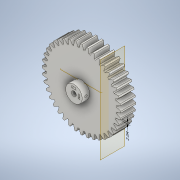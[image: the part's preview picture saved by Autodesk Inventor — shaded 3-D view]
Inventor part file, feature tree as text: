
AUTODESK INVENTOR PART (.ipt)
format: ipt  version: 2020 (Build 240168000, 168)  size: 377,344 bytes
history: native  units: mm (DEFAULTED — no unit token found)
features: sketch x7, extrude x6, other x5, plane x5
ambient origin geometry x8: Origin, YZ Plane, XZ Plane, XY Plane, X Axis, Y Axis, Z Axis, Center Point
bodies: Solid1 (feature_tree)
feature tree (23):
  other  "Annotations"
  extrude  "Extrusion1"  Depth=20.0mm TaperAngle=0.0deg
  plane  "Work Plane2"
  plane  "Work Plane8"
  plane  "Work Plane9"
  other  "Spur Gear"
  extrude  "Extrusion2"  Depth=10.0mm TaperAngle=0.0deg
  plane  "Work Plane13"
  extrude  "Extrusion3"  Depth=0.785398mm TaperAngle=0.0deg
  extrude  "Extrusion4"  TaperAngle=0.0deg  [1 undecoded]
  extrude  "Extrusion5"  Depth=62.5mm
  plane  "Work Plane14"
  sketch  "Sketch8"  dims[d47=0.0mm d48=0.0mm d49=22.0mm]
  extrude  "Extrusion6"  Depth=22.0mm
  sketch  "Sketch1"  dims[d0=105.0mm d1=20.0mm d2=0.0mm]
  sketch  "Sketch2"  dims[d3=100.0mm d4=10.0mm d5=0.0mm]
  other  "Srf1"
  sketch  "Sketch3"  dims[d16=62.5mm d17=0.0mm d34=0.785398mm]
  sketch  "Sketch5"  dims[d39=0.0mm d41=0.0mm]
  sketch  "Sketch6"  dims[d43=62.5mm d46=62.5mm]
  sketch  "Sketch9"  dims[d50=10.0mm d51=0.0mm d53=10.0mm d54=3.0mm d55=25.0mm d56=12.0mm d57=0.0mm d58=6.45mm d59=0.0mm d60=0.0mm d66=8.0mm d67=0.0mm d68=5.5mm d71=2.5mm d76=90.0deg d77=3.2mm d79=35.0mm d80=0.0mm d82=38.0mm d95=2.5mm d96=2.75mm d97=2.75mm d98=5.5mm d52=2.036157mm d81=0.5mm]
  other  "Pitch Diameter"
  other  "Linear Dimension 1"
note: 1 required parameter value undecoded (feature->parameter linkage not recoverable at this tier; creation-order binding heuristic only, values carry confidence <= 0.55)
